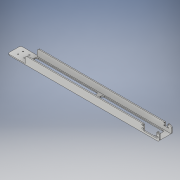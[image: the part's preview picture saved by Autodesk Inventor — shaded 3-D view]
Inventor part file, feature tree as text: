
AUTODESK INVENTOR PART (.ipt)
format: ipt  version: 2017 (Build 210142000, 142)  size: 280,064 bytes
history: native  units: in
note: dims shown in document units (in); Inventor stores cm internally (conversion verified against a paired STEP export)
features: sketch x6, extrude x5, projected_geometry x5, fillet x4, hole x1
ambient origin geometry x8: Origin, YZ Plane, XZ Plane, XY Plane, X Axis, Y Axis, Z Axis, Center Point
bodies: Solid1 (feature_tree)
feature tree (21):
  extrude  "Extrusion1"  Depth=1.685in
  extrude  "Extrusion2"  Depth=1.435in
  fillet  "Fillet1"  Radius=0.125in
  fillet  "Fillet2"  Radius=19.5in
  extrude  "Extrusion5"  Depth=1.0in
  fillet  "Fillet3"  Radius=0.75in
  extrude  "Extrusion6"  Depth=2.0in
  fillet  "Fillet4"  Radius=0.19in
  hole  "Hole1"  [1 undecoded]
  extrude  "Extrusion7"  Depth=0.25in
  sketch  "Sketch1"  dims[d0=1.0in d1=1.685in]
  sketch  "Sketch2"  dims[d2=0.875in d3=1.435in d4=0.125in d5=19.5in d6=0.0in]
  projected_geometry  "Projected Loop1"
  sketch  "Sketch6"  dims[d7=0.35in d8=1.0in d9=0.75in]
  projected_geometry  "Projected Loop4"
  sketch  "Sketch7"  dims[d10=2.0in d11=0.19in d12=0.19in]
  projected_geometry  "Projected Loop5"
  sketch  "Sketch8"  dims[d13=0.164in d14=0.3937in]
  projected_geometry  "Projected Loop6"
  sketch  "Sketch9"  dims[d15=0.19in d16=0.19in d19=0.5in d20=0.0in d26=0.197in d27=0.197in d28=1.9488in d29=1.9488in d30=0.3937in d43=0.125in d44=0.25in d46=2.25in d47=0.875in d48=5.0in d49=0.0in d50=0.25in d52=1.685in d53=0.25in d54=0.25in d55=2.25in d56=17.0in d57=8.0in d58=8.0in d59=0.25in d60=0.25in d61=0.5in d62=5.0in d63=0.0in d64=0.25in d70=0.8051in d71=0.6299in d72=0.4772in d73=0.7785in d74=0.1457in d75=0.75in d76=0.375in d77=0.25in d78=0.5635in d79=1.0in d80=0.8108in d97=0.097in d98=0.097in d99=0.097in d100=0.097in d101=0.376in d102=0.376in d103=0.546in d104=0.546in d105=0.936in d106=0.621in d107=0.621in d108=0.936in d109=0.3937in d110=0.423in d111=0.0761in d112=0.25in d113=0.0in]
  projected_geometry  "Projected Loop7"
note: 1 required parameter value undecoded (feature->parameter linkage not recoverable at this tier; creation-order binding heuristic only, values carry confidence <= 0.55)
